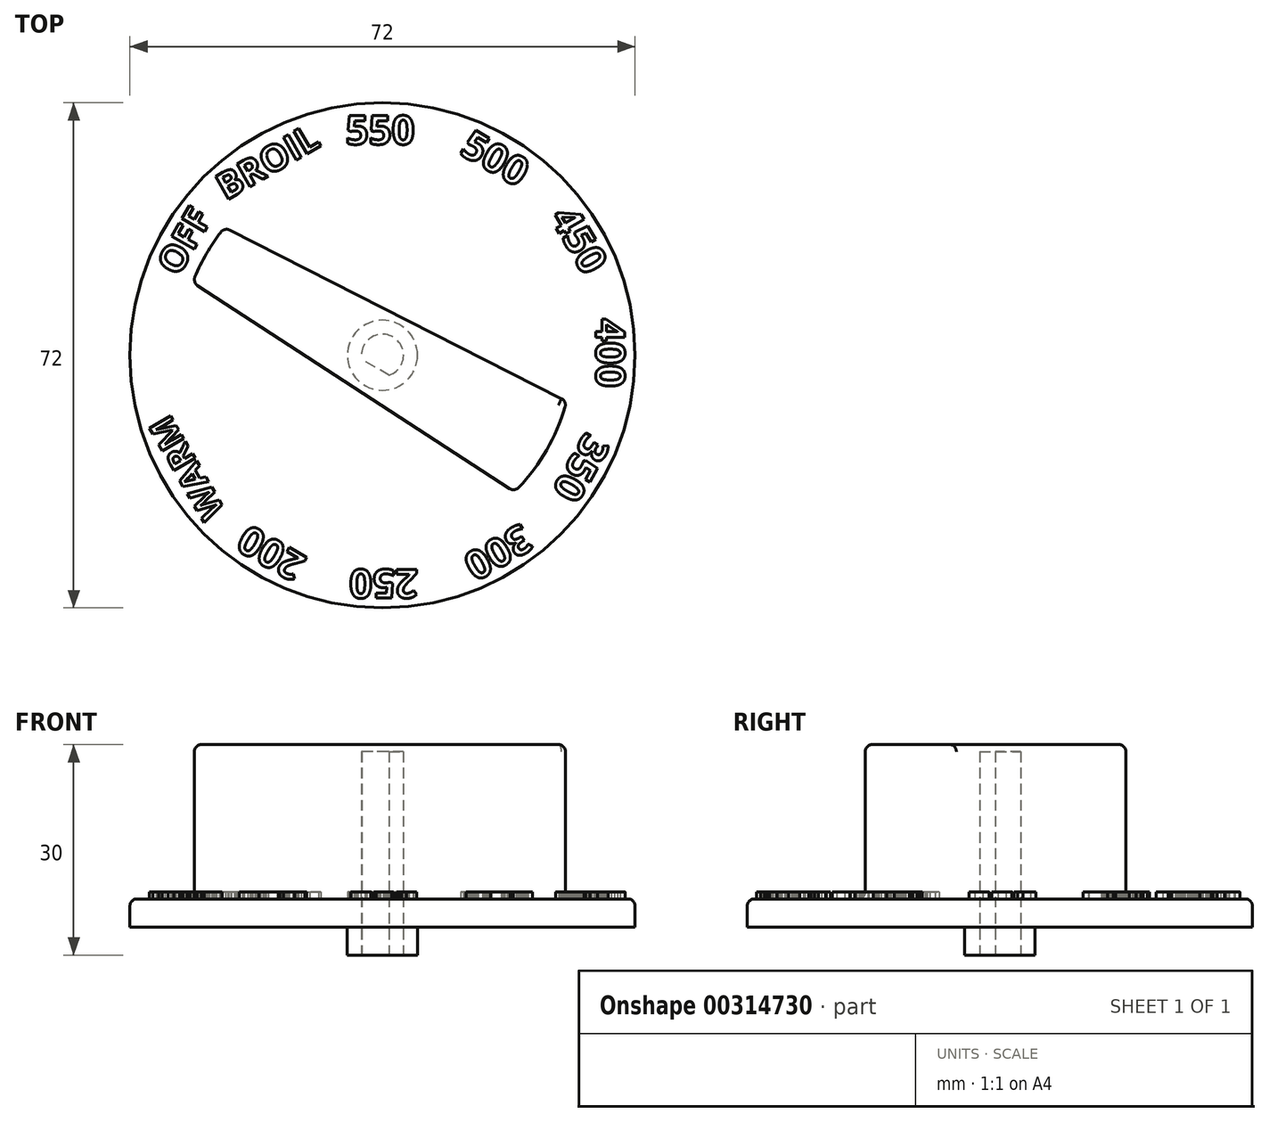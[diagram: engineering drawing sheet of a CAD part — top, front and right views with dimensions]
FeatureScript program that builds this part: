
annotation { "Feature Type Name" : "Feature", "Feature Type Description" : "" }
export const myFeature = defineFeature(function(context is Context, id is Id, definition is map)
    precondition{}
    {
        {
            var Q0;
            Q0=qCreatedBy(makeId("Top.planeOp"),FACE);
            var sketch = newSketch(context, id + "F0", { "sketchPlane" : qUnion([Q0])});
            skCircle(sketch, "E0", {"center": v(0, 0) * mm, "radius": 36 * mm});
            skCircle(sketch, "E1", {"center": v(0, 0) * mm, "radius": 5 * mm});
            skArc(sketch, "E2", {"start": v(-2.24, 2) * mm, "mid": v(0, -3) * mm, "end": v(2.24, 2) * mm});
            skLineSegment(sketch, "E3", {"start": v(-2.24, 2) * mm, "end": v(2.24, 2) * mm});
            skLineSegment(sketch, "E4", {"start": v(-25.2, 7.4) * mm, "end": v(27.79, 4.56) * mm});
            skArc(sketch, "E5", {"start": v(-26.23, 6.64) * mm, "mid": v(-26.83, 3.34) * mm, "end": v(-27.03, 0) * mm});
            skArc(sketch, "E6.trimOffspring", {"start": v(28.97, 0) * mm, "mid": v(28.91, 1.85) * mm, "end": v(28.73, 3.7) * mm});
            skArc(sketch, "E7.filletArc", {"start": v(-25.2, 7.4) * mm, "mid": v(-25.85, 7.2) * mm, "end": v(-26.23, 6.64) * mm});
            skArc(sketch, "E8.filletArc", {"start": v(28.73, 3.7) * mm, "mid": v(28.41, 4.3) * mm, "end": v(27.79, 4.56) * mm});
            skLineSegment(sketch, "E9.MirrorCS", {"start": v(-25.2, -7.4) * mm, "end": v(27.79, -4.56) * mm});
            skArc(sketch, "E10.MirrorCS", {"start": v(-25.2, -7.4) * mm, "mid": v(-25.85, -7.2) * mm, "end": v(-26.23, -6.64) * mm});
            skArc(sketch, "E11.MirrorCS", {"start": v(-26.23, -6.64) * mm, "mid": v(-26.83, -3.34) * mm, "end": v(-27.03, 0) * mm});
            skArc(sketch, "E12.MirrorCS", {"start": v(28.97, 0) * mm, "mid": v(28.91, -1.85) * mm, "end": v(28.73, -3.7) * mm});
            skArc(sketch, "E13.MirrorCS", {"start": v(28.73, -3.7) * mm, "mid": v(28.41, -4.3) * mm, "end": v(27.79, -4.56) * mm});
            skSolve(sketch);
        }
        {
            var Q0;
            Q0=makeQuery(id+"F0.imprint","IMPRINT",FACE,{"disambiguationData":[TD([[makeQuery(id+"F0.imprint","IMPRINT",EDGE,{"derivedFrom":sQuery(id+"F0.wireOp",EDGE,"E0")}),1.0]])]});
            var Q1;
            Q1=makeQuery(id+"F0.imprint","IMPRINT",FACE,{"disambiguationData":[TD([[makeQuery(id+"F0.imprint","IMPRINT",EDGE,{"derivedFrom":sQuery(id+"F0.wireOp",EDGE,"E1")}),-1.0]])]});
            var Q2;
            Q2=makeQuery(id+"F0.imprint","IMPRINT",FACE,{"disambiguationData":[TD([[makeQuery(id+"F0.imprint","IMPRINT",EDGE,{"derivedFrom":sQuery(id+"F0.wireOp",EDGE,"E1")}),1.0]])]});
            var Q3;
            Q3=makeQuery(id+"F0.imprint","IMPRINT",FACE,{"disambiguationData":[TD([[makeQuery(id+"F0.imprint","IMPRINT",EDGE,{"derivedFrom":sQuery(id+"F0.wireOp",EDGE,"E2")}),1.0]])]});
            extrude(context, id + "F1", {"entities" : qUnion([Q0, Q1, Q2, Q3]), "depth" : 4 * mm});
        }
        {
            var Q0;
            Q0=makeQuery(id+"F0.imprint","IMPRINT",FACE,{"disambiguationData":[TD([[makeQuery(id+"F0.imprint","IMPRINT",EDGE,{"derivedFrom":sQuery(id+"F0.wireOp",EDGE,"E1")}),-1.0]])]});
            var Q1;
            Q1=makeQuery(id+"F0.imprint","IMPRINT",FACE,{"disambiguationData":[TD([[makeQuery(id+"F0.imprint","IMPRINT",EDGE,{"derivedFrom":sQuery(id+"F0.wireOp",EDGE,"E2")}),1.0]])]});
            var Q2;
            Q2=makeQuery(id+"F0.imprint","IMPRINT",FACE,{"disambiguationData":[TD([[makeQuery(id+"F0.imprint","IMPRINT",EDGE,{"derivedFrom":sQuery(id+"F0.wireOp",EDGE,"E1")}),1.0]])]});
            extrude(context, id + "F2", {"entities" : qUnion([Q0, Q1, Q2]), "operationType" : NewBodyOperationType.ADD, "depth" : 26 * mm});
        }
        {
            var Q0;
            Q0=makeQuery(id+"F2.opExtrude","CAP_EDGE",EDGE,{"disambiguationData":[OSD([sQuery(id+"F0.wireOp",EDGE,"E4")])],"isStart":false});
            var Q1;
            Q1=makeQuery(id+"F2.opExtrude","CAP_EDGE",EDGE,{"disambiguationData":[OSD([sQuery(id+"F0.wireOp",EDGE,"E8.filletArc")])],"isStart":false});
            var Q2;
            Q2=makeQuery(id+"F2.opExtrude","CAP_EDGE",EDGE,{"disambiguationData":[OSD([sQuery(id+"F0.wireOp",EDGE,"E9.MirrorCS")])],"isStart":false});
            var Q3;
            Q3=makeQuery(id+"F2.opExtrude","CAP_FACE",FACE,{"disambiguationData":[OSD([sQuery(id+"F0.wireOp",EDGE,"E4"),sQuery(id+"F0.wireOp",EDGE,"E5"),sQuery(id+"F0.wireOp",EDGE,"E6.trimOffspring"),sQuery(id+"F0.wireOp",EDGE,"E7.filletArc"),sQuery(id+"F0.wireOp",EDGE,"E8.filletArc"),sQuery(id+"F0.wireOp",EDGE,"E9.MirrorCS"),sQuery(id+"F0.wireOp",EDGE,"E10.MirrorCS"),sQuery(id+"F0.wireOp",EDGE,"E11.MirrorCS"),sQuery(id+"F0.wireOp",EDGE,"E12.MirrorCS"),sQuery(id+"F0.wireOp",EDGE,"E13.MirrorCS")])],"isStart":false});
            fillet(context, id + "F3", {"entities" : qUnion([Q0, Q1, Q2, Q3]), "radius" : 1 * mm, "tangentPropagation" : true, "allowEdgeOverflow" : false});
        }
        {
            var Q0;
            Q0=makeQuery(id+"F0.imprint","IMPRINT",FACE,{"disambiguationData":[TD([[makeQuery(id+"F0.imprint","IMPRINT",EDGE,{"derivedFrom":sQuery(id+"F0.wireOp",EDGE,"E2")}),1.0]])]});
            extrude(context, id + "F4", {"entities" : qUnion([Q0]), "operationType" : NewBodyOperationType.REMOVE, "depth" : 25 * mm});
        }
        {
            var Q0;
            Q0=makeQuery(id+"F1.opExtrude","CAP_FACE",FACE,{"disambiguationData":[OSD([sQuery(id+"F0.wireOp",EDGE,"E0")])],"isStart":false});
            fillet(context, id + "F5", {"entities" : qUnion([Q0]), "radius" : 1 * mm, "tangentPropagation" : true, "allowEdgeOverflow" : false});
        }
        {
            var Q0;
            Q0=makeQuery(id+"F0.imprint","IMPRINT",FACE,{"disambiguationData":[TD([[makeQuery(id+"F0.imprint","IMPRINT",EDGE,{"derivedFrom":sQuery(id+"F0.wireOp",EDGE,"E1")}),1.0]])]});
            extrude(context, id + "F6", {"entities" : qUnion([Q0]), "operationType" : NewBodyOperationType.ADD, "oppositeDirection" : true, "depth" : 4 * mm});
        }
        {
            var Q0;
            Q0=qCreatedBy(makeId("Front.planeOp"),FACE);
            var sketch = newSketch(context, id + "F7", { "sketchPlane" : qUnion([Q0])});
            skLineSegment(sketch, "E14", {"start": v(0, 75.34) * mm, "end": v(0, 0) * mm});
            skSolve(sketch);
        }
        {
            var Q0;
            Q0=makeQuery(id+"F1.opExtrude","SWEPT_BODY",BODY,{"disambiguationData":[OSD([sQuery(id+"F0.wireOp",EDGE,"E0")])]});
            var Q1;
            Q1=sQuery(id+"F7.wireOp",EDGE,"E14");
            transform(context, id + "F8", {"entities" : qUnion([Q0]), "transformType" : TransformType.ROTATION, "transformAxis" : qUnion([Q1]), "angle" : 90 * degree, "oppositeDirection" : true, "makeCopy" : false});
        }
        {
            var Q0;
            Q0=makeQuery(id+"F1.opExtrude","CAP_FACE",FACE,{"disambiguationData":[OSD([sQuery(id+"F0.wireOp",EDGE,"E0")])],"isStart":false});
            var sketch = newSketch(context, id + "F9", { "sketchPlane" : qUnion([Q0])});
            skText(sketch, "E15", { "text": "OFF\n", "fontName": "OpenSans-Bold.ttf"});
            const initialGuessF9  = {"E15": [-0.00494, 0.03077, 1, 0, 0.00377]};
            skSetInitialGuess(sketch, initialGuessF9);
            skSolve(sketch);
        }
        {
            var Q0;
            Q0 = qSketchRegion(id + "F9", true);
            extrude(context, id + "F10", {"entities" : qUnion([Q0]), "operationType" : NewBodyOperationType.ADD, "depth" : 1 * mm});
        }
        {
            var Q0;
            Q0=makeQuery(id+"F1.opExtrude","SWEPT_BODY",BODY,{"disambiguationData":[OSD([sQuery(id+"F0.wireOp",EDGE,"E0")])]});
            var Q1;
            Q1=sQuery(id+"F7.wireOp",EDGE,"E14");
            transform(context, id + "F11", {"entities" : qUnion([Q0]), "transformType" : TransformType.ROTATION, "transformAxis" : qUnion([Q1]), "angle" : 90 * degree, "makeCopy" : false});
        }
        {
            var Q0;
            {var subQ0=sQuery(id+"F0.wireOp",EDGE,"E0");Q0=makeQuery(id+"F10.boolean.opBoolean","SPLIT",FACE,{"disambiguationData":[TD([makeQuery(id+"F5.opFillet","BLEND_FACE",FACE,{"disambiguationData":[OSD([subQ0])]})])],"derivedFrom":makeQuery(id+"F1.opExtrude","CAP_FACE",FACE,{"disambiguationData":[OSD([subQ0])],"isStart":false})});}
            var sketch = newSketch(context, id + "F12", { "sketchPlane" : qUnion([Q0])});
            skText(sketch, "E16", { "text": "200", "fontName": "OpenSans-Bold.ttf"});
            const initialGuessF12  = {"E16": [-0.00529, 0.03033, 1, 0, 0.00413]};
            skSetInitialGuess(sketch, initialGuessF12);
            skSolve(sketch);
        }
        {
            var Q0;
            Q0 = qSketchRegion(id + "F12", true);
            extrude(context, id + "F13", {"entities" : qUnion([Q0]), "operationType" : NewBodyOperationType.ADD, "depth" : 1 * mm});
        }
        {
            var Q0;
            Q0=makeQuery(id+"F1.opExtrude","SWEPT_BODY",BODY,{"disambiguationData":[OSD([sQuery(id+"F0.wireOp",EDGE,"E0")])]});
            var Q1;
            Q1=sQuery(id+"F7.wireOp",EDGE,"E14");
            transform(context, id + "F14", {"entities" : qUnion([Q0]), "transformType" : TransformType.ROTATION, "transformAxis" : qUnion([Q1]), "angle" : 30 * degree, "makeCopy" : false});
        }
        {
            var Q0;
            {var subQ16=sQuery(id+"F0.wireOp",EDGE,"E0");var subQ19=makeQuery(id+"F5.opFillet","BLEND_FACE",FACE,{"disambiguationData":[OSD([subQ16])]});Q0=makeQuery(id+"F13.boolean.opBoolean","SPLIT",FACE,{"disambiguationData":[TD([subQ19])],"derivedFrom":makeQuery(id+"F10.boolean.opBoolean","SPLIT",FACE,{"disambiguationData":[TD([subQ19])],"derivedFrom":makeQuery(id+"F1.opExtrude","CAP_FACE",FACE,{"disambiguationData":[OSD([subQ16])],"isStart":false})})});}
            var sketch = newSketch(context, id + "F15", { "sketchPlane" : qUnion([Q0])});
            skText(sketch, "E17", { "text": "250", "fontName": "OpenSans-Bold.ttf"});
            const initialGuessF15  = {"E17": [-0.0051, 0.03052, 1, 0, 0.00413]};
            skSetInitialGuess(sketch, initialGuessF15);
            skSolve(sketch);
        }
        {
            var Q0;
            Q0 = qSketchRegion(id + "F15", true);
            extrude(context, id + "F16", {"entities" : qUnion([Q0]), "operationType" : NewBodyOperationType.ADD, "depth" : 1 * mm});
        }
        {
            var Q0;
            Q0=makeQuery(id+"F1.opExtrude","SWEPT_BODY",BODY,{"disambiguationData":[OSD([sQuery(id+"F0.wireOp",EDGE,"E0")])]});
            var Q1;
            Q1=sQuery(id+"F7.wireOp",EDGE,"E14");
            transform(context, id + "F17", {"entities" : qUnion([Q0]), "transformType" : TransformType.ROTATION, "transformAxis" : qUnion([Q1]), "angle" : 30 * degree, "makeCopy" : false});
        }
        {
            var Q0;
            {var subQ27=sQuery(id+"F0.wireOp",EDGE,"E0");var subQ48=makeQuery(id+"F5.opFillet","BLEND_FACE",FACE,{"disambiguationData":[OSD([subQ27])]});Q0=makeQuery(id+"F16.boolean.opBoolean","SPLIT",FACE,{"disambiguationData":[TD([subQ48])],"derivedFrom":makeQuery(id+"F13.boolean.opBoolean","SPLIT",FACE,{"disambiguationData":[TD([subQ48])],"derivedFrom":makeQuery(id+"F10.boolean.opBoolean","SPLIT",FACE,{"disambiguationData":[TD([subQ48])],"derivedFrom":makeQuery(id+"F1.opExtrude","CAP_FACE",FACE,{"disambiguationData":[OSD([subQ27])],"isStart":false})})})});}
            var sketch = newSketch(context, id + "F18", { "sketchPlane" : qUnion([Q0])});
            skText(sketch, "E18", { "text": "300", "fontName": "OpenSans-Bold.ttf"});
            const initialGuessF18  = {"E18": [-0.00515, 0.03053, 1, 0, 0.00413]};
            skSetInitialGuess(sketch, initialGuessF18);
            skSolve(sketch);
        }
        {
            var Q0;
            Q0 = qSketchRegion(id + "F18", true);
            extrude(context, id + "F19", {"entities" : qUnion([Q0]), "operationType" : NewBodyOperationType.ADD, "depth" : 1 * mm});
        }
        {
            var Q0;
            Q0=makeQuery(id+"F1.opExtrude","SWEPT_BODY",BODY,{"disambiguationData":[OSD([sQuery(id+"F0.wireOp",EDGE,"E0")])]});
            var Q1;
            Q1=sQuery(id+"F7.wireOp",EDGE,"E14");
            transform(context, id + "F20", {"entities" : qUnion([Q0]), "transformType" : TransformType.ROTATION, "transformAxis" : qUnion([Q1]), "angle" : 30 * degree, "makeCopy" : false});
        }
        {
            var Q0;
            {var subQ45=sQuery(id+"F0.wireOp",EDGE,"E0");var subQ71=makeQuery(id+"F5.opFillet","BLEND_FACE",FACE,{"disambiguationData":[OSD([subQ45])]});Q0=makeQuery(id+"F19.boolean.opBoolean","SPLIT",FACE,{"disambiguationData":[TD([subQ71])],"derivedFrom":makeQuery(id+"F16.boolean.opBoolean","SPLIT",FACE,{"disambiguationData":[TD([subQ71])],"derivedFrom":makeQuery(id+"F13.boolean.opBoolean","SPLIT",FACE,{"disambiguationData":[TD([subQ71])],"derivedFrom":makeQuery(id+"F10.boolean.opBoolean","SPLIT",FACE,{"disambiguationData":[TD([subQ71])],"derivedFrom":makeQuery(id+"F1.opExtrude","CAP_FACE",FACE,{"disambiguationData":[OSD([subQ45])],"isStart":false})})})})});}
            var sketch = newSketch(context, id + "F21", { "sketchPlane" : qUnion([Q0])});
            skText(sketch, "E19", { "text": "350", "fontName": "OpenSans-Bold.ttf"});
            const initialGuessF21  = {"E19": [-0.00514, 0.03053, 1, 0, 0.00413]};
            skSetInitialGuess(sketch, initialGuessF21);
            skSolve(sketch);
        }
        {
            var Q0;
            Q0 = qSketchRegion(id + "F21", true);
            extrude(context, id + "F22", {"entities" : qUnion([Q0]), "operationType" : NewBodyOperationType.ADD, "depth" : 1 * mm});
        }
        {
            var Q0;
            Q0=makeQuery(id+"F1.opExtrude","SWEPT_BODY",BODY,{"disambiguationData":[OSD([sQuery(id+"F0.wireOp",EDGE,"E0")])]});
            var Q1;
            Q1=sQuery(id+"F7.wireOp",EDGE,"E14");
            transform(context, id + "F23", {"entities" : qUnion([Q0]), "transformType" : TransformType.ROTATION, "transformAxis" : qUnion([Q1]), "angle" : 30 * degree, "makeCopy" : false});
        }
        {
            var Q0;
            {var subQ100=sQuery(id+"F0.wireOp",EDGE,"E0");var subQ123=makeQuery(id+"F5.opFillet","BLEND_FACE",FACE,{"disambiguationData":[OSD([subQ100])]});Q0=makeQuery(id+"F22.boolean.opBoolean","SPLIT",FACE,{"disambiguationData":[TD([subQ123])],"derivedFrom":makeQuery(id+"F19.boolean.opBoolean","SPLIT",FACE,{"disambiguationData":[TD([subQ123])],"derivedFrom":makeQuery(id+"F16.boolean.opBoolean","SPLIT",FACE,{"disambiguationData":[TD([subQ123])],"derivedFrom":makeQuery(id+"F13.boolean.opBoolean","SPLIT",FACE,{"disambiguationData":[TD([subQ123])],"derivedFrom":makeQuery(id+"F10.boolean.opBoolean","SPLIT",FACE,{"disambiguationData":[TD([subQ123])],"derivedFrom":makeQuery(id+"F1.opExtrude","CAP_FACE",FACE,{"disambiguationData":[OSD([subQ100])],"isStart":false})})})})})});}
            var sketch = newSketch(context, id + "F24", { "sketchPlane" : qUnion([Q0])});
            skText(sketch, "E20", { "text": "400", "fontName": "OpenSans-Bold.ttf"});
            const initialGuessF24  = {"E20": [-0.00522, 0.03043, 1, 0, 0.00413]};
            skSetInitialGuess(sketch, initialGuessF24);
            skSolve(sketch);
        }
        {
            var Q0;
            Q0 = qSketchRegion(id + "F24", true);
            extrude(context, id + "F25", {"entities" : qUnion([Q0]), "operationType" : NewBodyOperationType.ADD, "depth" : 1 * mm});
        }
        {
            var Q0;
            Q0=makeQuery(id+"F1.opExtrude","SWEPT_BODY",BODY,{"disambiguationData":[OSD([sQuery(id+"F0.wireOp",EDGE,"E0")])]});
            var Q1;
            Q1=sQuery(id+"F7.wireOp",EDGE,"E14");
            transform(context, id + "F26", {"entities" : qUnion([Q0]), "transformType" : TransformType.ROTATION, "transformAxis" : qUnion([Q1]), "angle" : 30 * degree, "makeCopy" : false});
        }
        {
            var Q0;
            {var subQ121=sQuery(id+"F0.wireOp",EDGE,"E0");var subQ146=makeQuery(id+"F5.opFillet","BLEND_FACE",FACE,{"disambiguationData":[OSD([subQ121])]});Q0=makeQuery(id+"F25.boolean.opBoolean","SPLIT",FACE,{"disambiguationData":[TD([subQ146])],"derivedFrom":makeQuery(id+"F22.boolean.opBoolean","SPLIT",FACE,{"disambiguationData":[TD([subQ146])],"derivedFrom":makeQuery(id+"F19.boolean.opBoolean","SPLIT",FACE,{"disambiguationData":[TD([subQ146])],"derivedFrom":makeQuery(id+"F16.boolean.opBoolean","SPLIT",FACE,{"disambiguationData":[TD([subQ146])],"derivedFrom":makeQuery(id+"F13.boolean.opBoolean","SPLIT",FACE,{"disambiguationData":[TD([subQ146])],"derivedFrom":makeQuery(id+"F10.boolean.opBoolean","SPLIT",FACE,{"disambiguationData":[TD([subQ146])],"derivedFrom":makeQuery(id+"F1.opExtrude","CAP_FACE",FACE,{"disambiguationData":[OSD([subQ121])],"isStart":false})})})})})})});}
            var sketch = newSketch(context, id + "F27", { "sketchPlane" : qUnion([Q0])});
            skText(sketch, "E21", { "text": "450", "fontName": "OpenSans-Bold.ttf"});
            const initialGuessF27  = {"E21": [-0.00513, 0.03049, 1, 0, 0.00413]};
            skSetInitialGuess(sketch, initialGuessF27);
            skSolve(sketch);
        }
        {
            var Q0;
            Q0 = qSketchRegion(id + "F27", true);
            extrude(context, id + "F28", {"entities" : qUnion([Q0]), "operationType" : NewBodyOperationType.ADD, "depth" : 1 * mm});
        }
        {
            var Q0;
            Q0=makeQuery(id+"F1.opExtrude","SWEPT_BODY",BODY,{"disambiguationData":[OSD([sQuery(id+"F0.wireOp",EDGE,"E0")])]});
            var Q1;
            Q1=sQuery(id+"F7.wireOp",EDGE,"E14");
            transform(context, id + "F29", {"entities" : qUnion([Q0]), "transformType" : TransformType.ROTATION, "transformAxis" : qUnion([Q1]), "angle" : 30 * degree, "makeCopy" : false});
        }
        {
            var Q0;
            {var subQ137=sQuery(id+"F0.wireOp",EDGE,"E0");var subQ162=makeQuery(id+"F5.opFillet","BLEND_FACE",FACE,{"disambiguationData":[OSD([subQ137])]});Q0=makeQuery(id+"F28.boolean.opBoolean","SPLIT",FACE,{"disambiguationData":[TD([subQ162])],"derivedFrom":makeQuery(id+"F25.boolean.opBoolean","SPLIT",FACE,{"disambiguationData":[TD([subQ162])],"derivedFrom":makeQuery(id+"F22.boolean.opBoolean","SPLIT",FACE,{"disambiguationData":[TD([subQ162])],"derivedFrom":makeQuery(id+"F19.boolean.opBoolean","SPLIT",FACE,{"disambiguationData":[TD([subQ162])],"derivedFrom":makeQuery(id+"F16.boolean.opBoolean","SPLIT",FACE,{"disambiguationData":[TD([subQ162])],"derivedFrom":makeQuery(id+"F13.boolean.opBoolean","SPLIT",FACE,{"disambiguationData":[TD([subQ162])],"derivedFrom":makeQuery(id+"F10.boolean.opBoolean","SPLIT",FACE,{"disambiguationData":[TD([subQ162])],"derivedFrom":makeQuery(id+"F1.opExtrude","CAP_FACE",FACE,{"disambiguationData":[OSD([subQ137])],"isStart":false})})})})})})})});}
            var sketch = newSketch(context, id + "F30", { "sketchPlane" : qUnion([Q0])});
            skText(sketch, "E22", { "text": "500", "fontName": "OpenSans-Bold.ttf"});
            const initialGuessF30  = {"E22": [-0.00502, 0.03034, 1, 0, 0.00413]};
            skSetInitialGuess(sketch, initialGuessF30);
            skSolve(sketch);
        }
        {
            var Q0;
            Q0 = qSketchRegion(id + "F30", true);
            extrude(context, id + "F31", {"entities" : qUnion([Q0]), "operationType" : NewBodyOperationType.ADD, "depth" : 1 * mm});
        }
        {
            var Q0;
            Q0=makeQuery(id+"F1.opExtrude","SWEPT_BODY",BODY,{"disambiguationData":[OSD([sQuery(id+"F0.wireOp",EDGE,"E0")])]});
            var Q1;
            Q1=sQuery(id+"F7.wireOp",EDGE,"E14");
            transform(context, id + "F32", {"entities" : qUnion([Q0]), "transformType" : TransformType.ROTATION, "transformAxis" : qUnion([Q1]), "angle" : 60 * degree, "makeCopy" : false});
        }
        {
            var Q0;
            {var subQ138=sQuery(id+"F0.wireOp",EDGE,"E0");var subQ163=makeQuery(id+"F5.opFillet","BLEND_FACE",FACE,{"disambiguationData":[OSD([subQ138])]});Q0=makeQuery(id+"F31.boolean.opBoolean","SPLIT",FACE,{"disambiguationData":[TD([subQ163])],"derivedFrom":makeQuery(id+"F28.boolean.opBoolean","SPLIT",FACE,{"disambiguationData":[TD([subQ163])],"derivedFrom":makeQuery(id+"F25.boolean.opBoolean","SPLIT",FACE,{"disambiguationData":[TD([subQ163])],"derivedFrom":makeQuery(id+"F22.boolean.opBoolean","SPLIT",FACE,{"disambiguationData":[TD([subQ163])],"derivedFrom":makeQuery(id+"F19.boolean.opBoolean","SPLIT",FACE,{"disambiguationData":[TD([subQ163])],"derivedFrom":makeQuery(id+"F16.boolean.opBoolean","SPLIT",FACE,{"disambiguationData":[TD([subQ163])],"derivedFrom":makeQuery(id+"F13.boolean.opBoolean","SPLIT",FACE,{"disambiguationData":[TD([subQ163])],"derivedFrom":makeQuery(id+"F10.boolean.opBoolean","SPLIT",FACE,{"disambiguationData":[TD([subQ163])],"derivedFrom":makeQuery(id+"F1.opExtrude","CAP_FACE",FACE,{"disambiguationData":[OSD([subQ138])],"isStart":false})})})})})})})})});}
            var sketch = newSketch(context, id + "F33", { "sketchPlane" : qUnion([Q0])});
            skText(sketch, "E23", { "text": "BROIL", "fontName": "OpenSans-Bold.ttf"});
            const initialGuessF33  = {"E23": [-0.00831, 0.03023, 1, 0, 0.00377]};
            skSetInitialGuess(sketch, initialGuessF33);
            skSolve(sketch);
        }
        {
            var Q0;
            Q0 = qSketchRegion(id + "F33", true);
            extrude(context, id + "F34", {"entities" : qUnion([Q0]), "operationType" : NewBodyOperationType.ADD, "depth" : 1 * mm});
        }
        {
            var Q0;
            Q0=makeQuery(id+"F1.opExtrude","SWEPT_BODY",BODY,{"disambiguationData":[OSD([sQuery(id+"F0.wireOp",EDGE,"E0")])]});
            var Q1;
            Q1=sQuery(id+"F7.wireOp",EDGE,"E14");
            transform(context, id + "F35", {"entities" : qUnion([Q0]), "transformType" : TransformType.ROTATION, "transformAxis" : qUnion([Q1]), "angle" : 90 * degree, "makeCopy" : false});
        }
        {
            var Q0;
            {var subQ139=sQuery(id+"F0.wireOp",EDGE,"E0");var subQ164=makeQuery(id+"F5.opFillet","BLEND_FACE",FACE,{"disambiguationData":[OSD([subQ139])]});Q0=makeQuery(id+"F34.boolean.opBoolean","SPLIT",FACE,{"disambiguationData":[TD([subQ164])],"derivedFrom":makeQuery(id+"F31.boolean.opBoolean","SPLIT",FACE,{"disambiguationData":[TD([subQ164])],"derivedFrom":makeQuery(id+"F28.boolean.opBoolean","SPLIT",FACE,{"disambiguationData":[TD([subQ164])],"derivedFrom":makeQuery(id+"F25.boolean.opBoolean","SPLIT",FACE,{"disambiguationData":[TD([subQ164])],"derivedFrom":makeQuery(id+"F22.boolean.opBoolean","SPLIT",FACE,{"disambiguationData":[TD([subQ164])],"derivedFrom":makeQuery(id+"F19.boolean.opBoolean","SPLIT",FACE,{"disambiguationData":[TD([subQ164])],"derivedFrom":makeQuery(id+"F16.boolean.opBoolean","SPLIT",FACE,{"disambiguationData":[TD([subQ164])],"derivedFrom":makeQuery(id+"F13.boolean.opBoolean","SPLIT",FACE,{"disambiguationData":[TD([subQ164])],"derivedFrom":makeQuery(id+"F10.boolean.opBoolean","SPLIT",FACE,{"disambiguationData":[TD([subQ164])],"derivedFrom":makeQuery(id+"F1.opExtrude","CAP_FACE",FACE,{"disambiguationData":[OSD([subQ139])],"isStart":false})})})})})})})})})});}
            var sketch = newSketch(context, id + "F36", { "sketchPlane" : qUnion([Q0])});
            skText(sketch, "E24", { "text": "WARM", "fontName": "OpenSans-Bold.ttf"});
            const initialGuessF36  = {"E24": [-0.00796, 0.03046, 1, 0, 0.00354]};
            skSetInitialGuess(sketch, initialGuessF36);
            skSolve(sketch);
        }
        {
            var Q0;
            Q0 = qSketchRegion(id + "F36", true);
            extrude(context, id + "F37", {"entities" : qUnion([Q0]), "operationType" : NewBodyOperationType.ADD, "depth" : 1 * mm});
        }
        {
            var Q0;
            Q0=makeQuery(id+"F1.opExtrude","SWEPT_BODY",BODY,{"disambiguationData":[OSD([sQuery(id+"F0.wireOp",EDGE,"E0")])]});
            var Q1;
            Q1=sQuery(id+"F7.wireOp",EDGE,"E14");
            transform(context, id + "F38", {"entities" : qUnion([Q0]), "transformType" : TransformType.ROTATION, "transformAxis" : qUnion([Q1]), "angle" : 120 * degree, "oppositeDirection" : true, "makeCopy" : false});
        }
        {
            var Q0;
            {var subQ312=sQuery(id+"F0.wireOp",EDGE,"E0");var subQ326=makeQuery(id+"F5.opFillet","BLEND_FACE",FACE,{"disambiguationData":[OSD([subQ312])]});Q0=makeQuery(id+"F37.boolean.opBoolean","SPLIT",FACE,{"disambiguationData":[TD([subQ326])],"derivedFrom":makeQuery(id+"F34.boolean.opBoolean","SPLIT",FACE,{"disambiguationData":[TD([subQ326])],"derivedFrom":makeQuery(id+"F31.boolean.opBoolean","SPLIT",FACE,{"disambiguationData":[TD([subQ326])],"derivedFrom":makeQuery(id+"F28.boolean.opBoolean","SPLIT",FACE,{"disambiguationData":[TD([subQ326])],"derivedFrom":makeQuery(id+"F25.boolean.opBoolean","SPLIT",FACE,{"disambiguationData":[TD([subQ326])],"derivedFrom":makeQuery(id+"F22.boolean.opBoolean","SPLIT",FACE,{"disambiguationData":[TD([subQ326])],"derivedFrom":makeQuery(id+"F19.boolean.opBoolean","SPLIT",FACE,{"disambiguationData":[TD([subQ326])],"derivedFrom":makeQuery(id+"F16.boolean.opBoolean","SPLIT",FACE,{"disambiguationData":[TD([subQ326])],"derivedFrom":makeQuery(id+"F13.boolean.opBoolean","SPLIT",FACE,{"disambiguationData":[TD([subQ326])],"derivedFrom":makeQuery(id+"F10.boolean.opBoolean","SPLIT",FACE,{"disambiguationData":[TD([subQ326])],"derivedFrom":makeQuery(id+"F1.opExtrude","CAP_FACE",FACE,{"disambiguationData":[OSD([subQ312])],"isStart":false})})})})})})})})})})});}
            var sketch = newSketch(context, id + "F39", { "sketchPlane" : qUnion([Q0])});
            skText(sketch, "E25", { "text": "550", "fontName": "OpenSans-Bold.ttf"});
            const initialGuessF39  = {"E25": [-0.00524, 0.03006, 1, 0, 0.00413]};
            skSetInitialGuess(sketch, initialGuessF39);
            skSolve(sketch);
        }
        {
            var Q0;
            Q0 = qSketchRegion(id + "F39", true);
            extrude(context, id + "F40", {"entities" : qUnion([Q0]), "operationType" : NewBodyOperationType.ADD, "depth" : 1 * mm});
        }
    });
